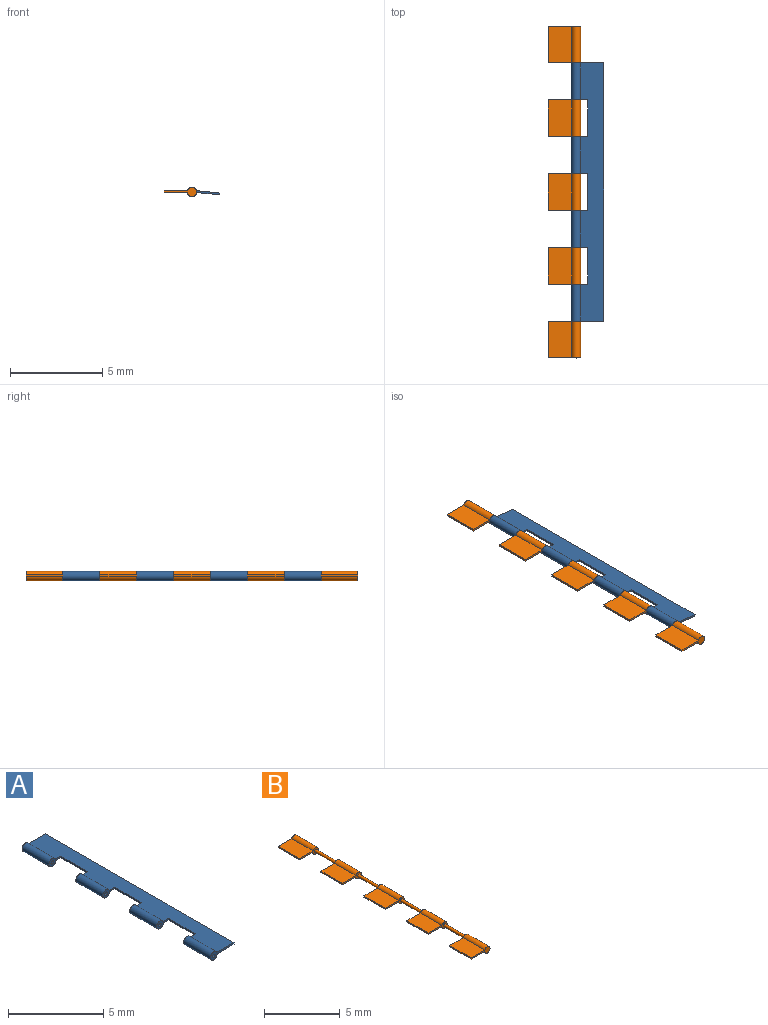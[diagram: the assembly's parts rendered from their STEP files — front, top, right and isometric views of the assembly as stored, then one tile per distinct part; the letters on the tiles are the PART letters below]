
ASSEMBLY  parts=2 mates=1
PART A: 22 faces, bbox 1.8x14x0.5 mm
  f0: plane 14x1.27mm, normal (0,0,1), area 15.4mm2, adj f2,f3,f5,f6,f7,f8,f10,f11
  f1: plane 14x1.25mm, normal (0,0,-1), area 15.2mm2, adj f2,f3,f5,f6,f7,f8,f10,f11
  f2: plane 1.75x0.5mm, normal (0,1,0), area 0.3mm2, adj f0,f1,f4,f5,f6
  f3: plane 0.88x0.5mm, normal (0,-1,0), area 0.2mm2, adj f0,f1,f4,f5,f19
  f4: cylinder r=0.1mm len=2mm, axis (0,-1,0), area 1.3mm2, adj f2,f3
  f5: cylinder r=0.25mm len=2mm, axis (0,-1,0), area 2.9mm2, adj f0,f1,f2,f3
  f6: plane 14x0.1mm, normal (1,0,0), area 1.4mm2, adj f0,f1,f2,f16
  f7: plane 0.88x0.5mm, normal (0,1,0), area 0.2mm2, adj f0,f1,f9,f10,f19
  f8: plane 0.88x0.5mm, normal (0,-1,0), area 0.2mm2, adj f0,f1,f9,f10,f20
  f9: cylinder r=0.1mm len=2mm, axis (0,-1,0), area 1.3mm2, adj f7,f8
  f10: cylinder r=0.25mm len=2mm, axis (0,-1,0), area 2.9mm2, adj f0,f1,f7,f8
  f11: plane 0.88x0.5mm, normal (0,1,0), area 0.2mm2, adj f0,f1,f13,f14,f20
  f12: plane 0.88x0.5mm, normal (0,-1,0), area 0.2mm2, adj f0,f1,f13,f14,f21
  f13: cylinder r=0.1mm len=2mm, axis (0,-1,0), area 1.3mm2, adj f11,f12
  f14: cylinder r=0.25mm len=2mm, axis (0,-1,0), area 2.9mm2, adj f0,f1,f11,f12
  f15: plane 0.88x0.5mm, normal (0,1,0), area 0.2mm2, adj f0,f1,f17,f18,f21
  f16: plane 1.75x0.5mm, normal (0,-1,0), area 0.3mm2, adj f0,f1,f6,f17,f18
  f17: cylinder r=0.1mm len=2mm, axis (0,-1,0), area 1.3mm2, adj f15,f16
  f18: cylinder r=0.25mm len=2mm, axis (0,-1,0), area 2.9mm2, adj f0,f1,f15,f16
  f19: plane 2x0.1mm, normal (-1,0,0), area 0.2mm2, adj f0,f1,f3,f7
  f20: plane 2x0.1mm, normal (-1,0,0), area 0.2mm2, adj f0,f1,f8,f11
  f21: plane 2x0.1mm, normal (-1,0,0), area 0.2mm2, adj f0,f1,f12,f15
PART B: 34 faces, bbox 1.8x18x0.5 mm
  f0: plane 1.75x0.5mm, normal (0,-1,0), area 0.3mm2, adj f2,f3,f4,f5
  f1: plane 1.75x0.5mm, normal (0,1,0), area 0.3mm2, adj f2,f3,f4,f5,f6
  f2: cylinder r=0.25mm len=2mm, axis (0,1,0), area 2.9mm2, adj f0,f1,f4,f5
  f3: plane 2x0.1mm, normal (-1,0,0), area 0.2mm2, adj f0,f1,f4,f5
  f4: plane 2x1.27mm, normal (0,0,1), area 2.5mm2, adj f0,f1,f2,f3
  f5: plane 2x1.25mm, normal (0,0,-1), area 2.5mm2, adj f0,f1,f2,f3
  f6: cylinder r=0.1mm len=2mm, axis (0,1,0), area 1.3mm2, adj f1,f31
  f7: plane 2x1.27mm, normal (0,0,1), area 2.5mm2, adj f8,f10,f11,f12
  f8: plane 2x0.1mm, normal (-1,0,0), area 0.2mm2, adj f7,f9,f10,f12
  f9: plane 2x1.25mm, normal (0,0,-1), area 2.5mm2, adj f8,f10,f11,f12
  f10: plane 1.75x0.5mm, normal (0,-1,0), area 0.3mm2, adj f7,f8,f9,f11,f13
  f11: cylinder r=0.25mm len=2mm, axis (0,1,0), area 2.9mm2, adj f7,f9,f10,f12
  f12: plane 1.75x0.5mm, normal (0,1,0), area 0.3mm2, adj f7,f8,f9,f11
  f13: cylinder r=0.1mm len=2mm, axis (0,1,0), area 1.3mm2, adj f10,f19
  f14: plane 2x1.27mm, normal (0,0,1), area 2.5mm2, adj f15,f17,f18,f19
  f15: plane 2x0.1mm, normal (-1,0,0), area 0.2mm2, adj f14,f16,f17,f19
  f16: plane 2x1.25mm, normal (0,0,-1), area 2.5mm2, adj f15,f17,f18,f19
  f17: plane 1.75x0.5mm, normal (0,-1,0), area 0.3mm2, adj f14,f15,f16,f18,f20
  f18: cylinder r=0.25mm len=2mm, axis (0,1,0), area 2.9mm2, adj f14,f16,f17,f19
  f19: plane 1.75x0.5mm, normal (0,1,0), area 0.3mm2, adj f13,f14,f15,f16,f18
  f20: cylinder r=0.1mm len=2mm, axis (0,1,0), area 1.3mm2, adj f17,f24
  f21: plane 2x1.25mm, normal (0,0,-1), area 2.5mm2, adj f22,f24,f25,f26
  f22: plane 2x0.1mm, normal (-1,0,0), area 0.2mm2, adj f21,f23,f24,f26
  f23: plane 2x1.27mm, normal (0,0,1), area 2.5mm2, adj f22,f24,f25,f26
  f24: plane 1.75x0.5mm, normal (0,1,0), area 0.3mm2, adj f20,f21,f22,f23,f25
  f25: cylinder r=0.25mm len=2mm, axis (0,1,0), area 2.9mm2, adj f21,f23,f24,f26
  f26: plane 1.75x0.5mm, normal (0,-1,0), area 0.3mm2, adj f21,f22,f23,f25,f27
  f27: cylinder r=0.1mm len=2mm, axis (0,1,0), area 1.3mm2, adj f26,f33
  f28: plane 2x1.27mm, normal (0,0,1), area 2.5mm2, adj f29,f31,f32,f33
  f29: plane 2x0.1mm, normal (-1,0,0), area 0.2mm2, adj f28,f30,f31,f33
  f30: plane 2x1.25mm, normal (0,0,-1), area 2.5mm2, adj f29,f31,f32,f33
  f31: plane 1.75x0.5mm, normal (0,-1,0), area 0.3mm2, adj f6,f28,f29,f30,f32
  f32: cylinder r=0.25mm len=2mm, axis (0,1,0), area 2.9mm2, adj f28,f30,f31,f33
  f33: plane 1.75x0.5mm, normal (0,1,0), area 0.3mm2, adj f27,f28,f29,f30,f32
PLACE A rot(axis=(0,1,0),5.9deg) t=(-2.57,-5.84,7.5)mm
PLACE B t=(-2.57,-5.84,7.5)mm fixed
MATE revolute A.f4 <-> B.f2  axis (0,-1,0) through (-2.57,-3.84,7.5)mm
